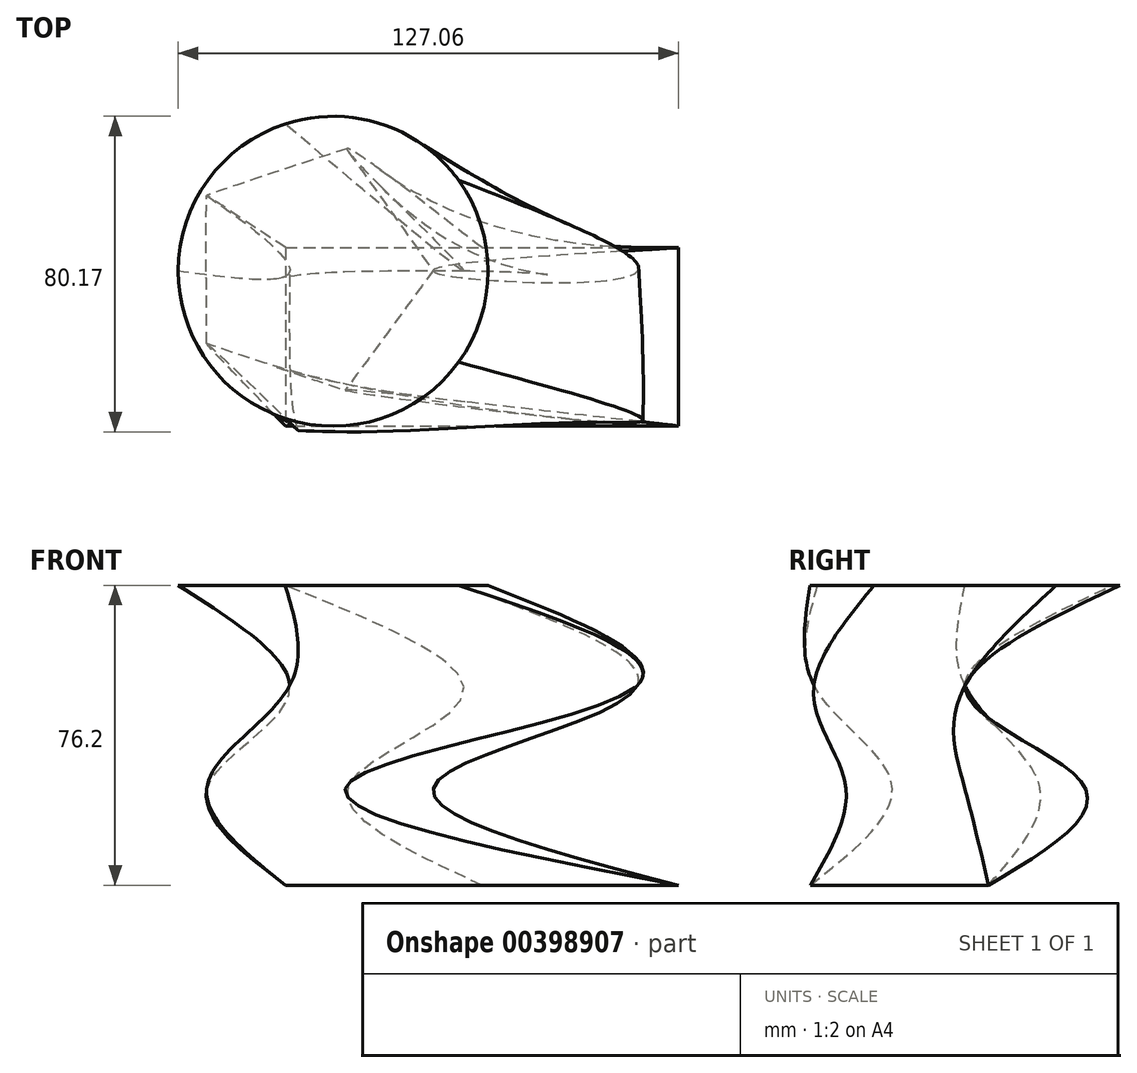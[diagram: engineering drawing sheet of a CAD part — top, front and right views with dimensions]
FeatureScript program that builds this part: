
annotation { "Feature Type Name" : "Feature", "Feature Type Description" : "" }
export const myFeature = defineFeature(function(context is Context, id is Id, definition is map)
    precondition{}
    {
        {
            var Q0;
            Q0=qCreatedBy(makeId("Top.planeOp"),FACE);
            cPlane(context, id + "F0", {"entities" : qUnion([Q0]), "cplaneType" : CPlaneType.OFFSET, "offset" : 25.4 * mm, "width" : 152.4 * mm, "height" : 152.4 * mm});
        }
        {
            var Q0;
            Q0=qCreatedBy(id+"F0.planeOp",FACE);
            cPlane(context, id + "F1", {"entities" : qUnion([Q0]), "cplaneType" : CPlaneType.OFFSET, "offset" : 25.4 * mm, "width" : 152.4 * mm, "height" : 152.4 * mm});
        }
        {
            var Q0;
            Q0=qCreatedBy(id+"F1.planeOp",FACE);
            cPlane(context, id + "F2", {"entities" : qUnion([Q0]), "cplaneType" : CPlaneType.OFFSET, "offset" : 25.4 * mm, "width" : 152.4 * mm, "height" : 152.4 * mm});
        }
        {
            var Q0;
            Q0=qCreatedBy(makeId("Top.planeOp"),FACE);
            var sketch = newSketch(context, id + "F3", { "sketchPlane" : qUnion([Q0])});
            skLineSegment(sketch, "E0.bottom", {"start": v(-37.28, 5.97) * mm, "end": v(62.54, 5.97) * mm});
            skLineSegment(sketch, "E0.top", {"start": v(-37.28, -39.33) * mm, "end": v(62.54, -39.33) * mm});
            skLineSegment(sketch, "E0.left", {"start": v(-37.28, 5.97) * mm, "end": v(-37.28, -39.33) * mm});
            skLineSegment(sketch, "E0.right", {"start": v(62.54, 5.97) * mm, "end": v(62.54, -39.33) * mm});
            skSolve(sketch);
        }
        {
            var Q0;
            Q0=qCreatedBy(id+"F0.planeOp",FACE);
            var sketch = newSketch(context, id + "F4", { "sketchPlane" : qUnion([Q0])});
            skCircle(sketch, "E1.cCircle", {"center": v(-31.27, 0) * mm, "radius": 25.75 * mm, "construction": true});
            skLineSegment(sketch, "E1.0", {"start": v(0.56, -0.25) * mm, "end": v(-21.67, -30.35) * mm});
            skLineSegment(sketch, "E1.1", {"start": v(-21.67, -30.35) * mm, "end": v(-57.16, -18.5) * mm});
            skLineSegment(sketch, "E1.2", {"start": v(-57.16, -18.5) * mm, "end": v(-56.87, 18.91) * mm});
            skLineSegment(sketch, "E1.3", {"start": v(-56.87, 18.91) * mm, "end": v(-21.2, 30.2) * mm});
            skLineSegment(sketch, "E1.4", {"start": v(-21.2, 30.2) * mm, "end": v(0.56, -0.25) * mm});
            skPoint(sketch, "E1.0.midPoint", {"position": v(-10.55, -15.3) * mm});
            skSolve(sketch);
        }
        {
            var Q0;
            Q0=qCreatedBy(id+"F1.planeOp",FACE);
            var sketch = newSketch(context, id + "F5", { "sketchPlane" : qUnion([Q0])});
            skLineSegment(sketch, "E2.bottom", {"start": v(-36.19, 0) * mm, "end": v(52.12, 0) * mm});
            skLineSegment(sketch, "E2.top", {"start": v(-36.19, -38.38) * mm, "end": v(52.12, -38.38) * mm});
            skLineSegment(sketch, "E2.left", {"start": v(-36.19, 0) * mm, "end": v(-36.19, -38.38) * mm});
            skLineSegment(sketch, "E2.right", {"start": v(52.12, 0) * mm, "end": v(52.12, -38.38) * mm});
            skSolve(sketch);
        }
        {
            var Q0;
            Q0=qCreatedBy(id+"F2.planeOp",FACE);
            var sketch = newSketch(context, id + "F6", { "sketchPlane" : qUnion([Q0])});
            skCircle(sketch, "E3", {"center": v(-25.17, 0) * mm, "radius": 39.36 * mm});
            skSolve(sketch);
        }
        {
            var Q0;
            Q0=makeQuery(id+"F3.imprint","IMPRINT",FACE,{"disambiguationData":[TD([[makeQuery(id+"F3.imprint","IMPRINT",EDGE,{"derivedFrom":sQuery(id+"F3.wireOp",EDGE,"E0.bottom")}),-1.0]])]});
            var Q1;
            Q1=makeQuery(id+"F4.imprint","IMPRINT",FACE,{"disambiguationData":[TD([[makeQuery(id+"F4.imprint","IMPRINT",EDGE,{"derivedFrom":sQuery(id+"F4.wireOp",EDGE,"E1.0")}),-1.0]])]});
            var Q2;
            Q2=makeQuery(id+"F5.imprint","IMPRINT",FACE,{"disambiguationData":[TD([[makeQuery(id+"F5.imprint","IMPRINT",EDGE,{"derivedFrom":sQuery(id+"F5.wireOp",EDGE,"E2.bottom")}),-1.0]])]});
            var Q3;
            Q3=makeQuery(id+"F6.imprint","IMPRINT",FACE,{"disambiguationData":[TD([[makeQuery(id+"F6.imprint","IMPRINT",EDGE,{"derivedFrom":sQuery(id+"F6.wireOp",EDGE,"E3")}),1.0]])]});
            loft(context, id + "F7", {"sheetProfilesArray" : [{ "sheetProfileEntities" : qUnion([Q0]) }, { "sheetProfileEntities" : qUnion([Q1]) }, { "sheetProfileEntities" : qUnion([Q2]) }, { "sheetProfileEntities" : qUnion([Q3]) }]});
        }
    });
